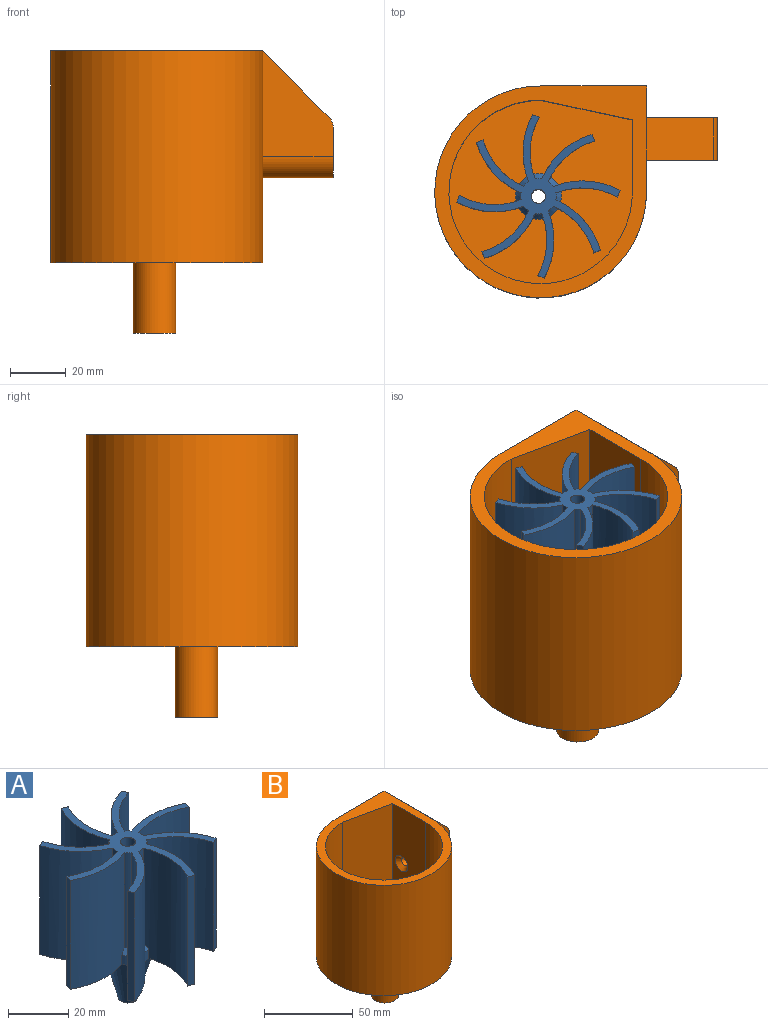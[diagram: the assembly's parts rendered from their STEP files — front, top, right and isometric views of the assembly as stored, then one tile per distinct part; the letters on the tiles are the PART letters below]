
ASSEMBLY  parts=2 mates=1
PART A: 60 faces, bbox 58.7x58.7x63.5 mm
  f0: cylinder r=28.57mm len=44.45mm, axis (0,0,-1), area 1098.7mm2, adj f18,f30,f31,f33,f48,f53
  f1: cylinder r=26.04mm len=44.45mm, axis (0,0,-1), area 1014.1mm2, adj f18,f24,f31,f33,f47,f54
  f2: cylinder r=28.57mm len=44.45mm, axis (0,0,-1), area 1098.7mm2, adj f29,f31,f34,f41,f49,f58
  f3: cylinder r=26.04mm len=44.45mm, axis (0,0,-1), area 1014.1mm2, adj f23,f31,f34,f41,f45,f57
  f4: cylinder r=28.57mm len=44.45mm, axis (0,0,-1), area 1098.7mm2, adj f20,f28,f31,f35,f46,f55
  f5: cylinder r=26.04mm len=44.45mm, axis (0,0,-1), area 1014.1mm2, adj f20,f27,f31,f35,f51,f56
  f6: cylinder r=28.57mm len=44.45mm, axis (0,0,-1), area 1098.7mm2, adj f21,f27,f31,f36,f51,f56
  f7: cylinder r=26.04mm len=44.45mm, axis (0,0,-1), area 1014.1mm2, adj f21,f26,f31,f36,f50,f59
  f8: cylinder r=28.57mm len=44.45mm, axis (0,0,-1), area 1098.7mm2, adj f22,f26,f31,f37,f50,f59
  f9: cylinder r=26.04mm len=44.45mm, axis (0,0,-1), area 1014.1mm2, adj f22,f29,f31,f37,f49,f58
  f10: cylinder r=28.57mm len=44.45mm, axis (0,0,-1), area 1098.7mm2, adj f17,f25,f31,f38,f44,f52
  f11: cylinder r=26.04mm len=44.45mm, axis (0,0,-1), area 1014.1mm2, adj f17,f30,f31,f38,f48,f53
  f12: cylinder r=28.57mm len=44.45mm, axis (0,0,-1), area 1098.7mm2, adj f19,f24,f31,f39,f47,f54
  f13: cylinder r=26.04mm len=44.45mm, axis (0,0,-1), area 1014.1mm2, adj f19,f28,f31,f39,f46,f55
  f14: cylinder r=28.57mm len=44.45mm, axis (0,0,-1), area 1098.7mm2, adj f16,f23,f31,f40,f45,f57
  f15: cylinder r=26.04mm len=44.45mm, axis (0,0,-1), area 1014.1mm2, adj f16,f25,f31,f40,f44,f52
  f16: plane 18.28x15.27mm, normal (0,0,-1), area 55.8mm2, adj f14,f15,f40,f43
  f17: plane 22.26x5.84mm, normal (0,0,-1), area 55.8mm2, adj f10,f11,f38,f43
  f18: plane 18.28x15.27mm, normal (0,0,-1), area 55.8mm2, adj f0,f1,f33,f43
  f19: plane 22.26x5.84mm, normal (0,0,-1), area 55.8mm2, adj f12,f13,f39,f43
  f20: plane 18.28x15.27mm, normal (0,0,-1), area 55.8mm2, adj f4,f5,f35,f43
  f21: plane 22.26x5.84mm, normal (0,0,-1), area 55.8mm2, adj f6,f7,f36,f43
  f22: plane 18.28x15.27mm, normal (0,0,-1), area 55.8mm2, adj f8,f9,f37,f43
  f23: cylinder r=6.35mm len=38.74mm, axis (0,0,-1), area 94.1mm2, adj f3,f14,f31,f57
  f24: cylinder r=6.35mm len=38.74mm, axis (0,0,-1), area 94.1mm2, adj f1,f12,f31,f54
  f25: cylinder r=6.35mm len=38.74mm, axis (0,0,-1), area 94.1mm2, adj f10,f15,f31,f52
  f26: cylinder r=6.35mm len=38.74mm, axis (0,0,-1), area 94.1mm2, adj f7,f8,f31,f59
  f27: cylinder r=6.35mm len=38.74mm, axis (0,0,-1), area 94.1mm2, adj f5,f6,f31,f56
  f28: cylinder r=6.35mm len=38.74mm, axis (0,0,-1), area 94.1mm2, adj f4,f13,f31,f55
  f29: cylinder r=6.35mm len=38.74mm, axis (0,0,-1), area 94.1mm2, adj f2,f9,f31,f58
  f30: cylinder r=6.35mm len=38.74mm, axis (0,0,-1), area 94.1mm2, adj f0,f11,f31,f53
  f31: plane 58.74x58.74mm, normal (0,0,1), area 591.8mm2, adj f0,f1,f2,f3,f4,f5,f6,f7
  f32: cylinder r=2.54mm len=63.5mm, axis (0,0,1), area 1013.4mm2, adj f31,f42
  f33: plane 44.45x2.34mm, normal (0.91,0.41,0), area 114mm2, adj f0,f1,f18,f31
  f34: plane 44.45x2.4mm, normal (-0.94,0.35,0), area 114mm2, adj f2,f3,f31,f41
  f35: plane 44.45x2.34mm, normal (0.41,-0.91,0), area 114mm2, adj f4,f5,f20,f31
  f36: plane 44.45x2.4mm, normal (-0.35,-0.94,0), area 114mm2, adj f6,f7,f21,f31
  f37: plane 44.45x2.34mm, normal (-0.91,-0.41,0), area 114mm2, adj f8,f9,f22,f31
  f38: plane 44.45x2.4mm, normal (0.35,0.94,0), area 114mm2, adj f10,f11,f17,f31
  f39: plane 44.45x2.4mm, normal (0.94,-0.35,0), area 114mm2, adj f12,f13,f19,f31
  f40: plane 44.45x2.34mm, normal (-0.41,0.91,0), area 114mm2, adj f14,f15,f16,f31
  f41: plane 22.26x5.84mm, normal (0,0,-1), area 55.8mm2, adj f2,f3,f34,f43
  f42: plane 6.35x6.35mm, normal (0,0,-1), area 11.4mm2, adj f32,f43
  f43: cone r=3.17mm half-angle=14.9deg, axis (0,0,1), area 708mm2, adj f16,f17,f18,f19,f20,f21,f22,f41
  f44: cylinder r=8.26mm len=3.81mm, axis (0,0,-1), area 15mm2, adj f10,f15,f43,f52
  f45: cylinder r=8.26mm len=3.89mm, axis (0,0,-1), area 15mm2, adj f3,f14,f43,f57
  f46: cylinder r=8.26mm len=3.89mm, axis (0,0,-1), area 15mm2, adj f4,f13,f43,f55
  f47: cylinder r=8.26mm len=3.81mm, axis (0,0,-1), area 15mm2, adj f1,f12,f43,f54
  f48: cylinder r=8.26mm len=3.89mm, axis (0,0,-1), area 15mm2, adj f0,f11,f43,f53
  f49: cylinder r=8.26mm len=3.81mm, axis (0,0,-1), area 15mm2, adj f2,f9,f43,f58
  f50: cylinder r=8.26mm len=3.89mm, axis (0,0,-1), area 15mm2, adj f7,f8,f43,f59
  f51: cylinder r=8.26mm len=3.81mm, axis (0,0,-1), area 15mm2, adj f5,f6,f43,f56
  f52: cone r=5.71mm half-angle=45deg, axis (0,0,-1), area 8.5mm2, adj f10,f15,f25,f44
  f53: cone r=5.71mm half-angle=45deg, axis (0,0,-1), area 8.5mm2, adj f0,f11,f30,f48
  f54: cone r=5.71mm half-angle=45deg, axis (0,0,-1), area 8.5mm2, adj f1,f12,f24,f47
  f55: cone r=5.71mm half-angle=45deg, axis (0,0,-1), area 8.5mm2, adj f4,f13,f28,f46
  f56: cone r=5.71mm half-angle=45deg, axis (0,0,-1), area 8.5mm2, adj f5,f6,f27,f51
  f57: cone r=5.71mm half-angle=45deg, axis (0,0,-1), area 8.5mm2, adj f3,f14,f23,f45
  f58: cone r=5.71mm half-angle=45deg, axis (0,0,-1), area 8.5mm2, adj f2,f9,f29,f49
  f59: cone r=5.71mm half-angle=45deg, axis (0,0,-1), area 8.5mm2, adj f7,f8,f26,f50
PART B: 22 faces, bbox 101.6x76.2x101.7 mm
  f0: plane 76.2x38.1mm, normal (1,0,0), area 2231.4mm2, adj f1,f3,f4,f5,f6,f17,f18
  f1: cylinder r=7.62mm len=25.4mm, axis (-1,0,0), area 608mm2, adj f0,f7,f17,f18
  f2: plane 71.12x25.91mm, normal (-1,0,0), area 1761.5mm2, adj f4,f9,f10,f14,f16
  f3: plane 76.2x38.1mm, normal (0,1,0), area 2903.2mm2, adj f0,f4,f5,f6
  f4: plane 76.2x76.2mm, normal (0,0,1), area 1330mm2, adj f0,f2,f3,f6,f9,f16,f19
  f5: plane 76.2x76.2mm, normal (0,0,-1), area 4689.5mm2, adj f0,f3,f6,f11
  f6: cylinder r=38.1mm len=76.2mm, axis (0,0,1), area 13681.1mm2, adj f0,f3,f4,f5
  f7: plane 18.27x15.24mm, normal (1,0,0), area 233.3mm2, adj f1,f8,f17,f18,f21
  f8: cylinder r=2.54mm len=27.94mm, axis (1,0,0), area 445.9mm2, adj f7,f14
  f9: cylinder r=33.02mm len=71.12mm, axis (0,0,1), area 11066.5mm2, adj f2,f4,f10,f16
  f10: plane 66.04x66.04mm, normal (0,0,1), area 3460.8mm2, adj f2,f9,f15,f16
  f11: cylinder r=7.62mm len=25.4mm, axis (0,0,1), area 1216.1mm2, adj f5,f12
  f12: plane 15.24x15.24mm, normal (0,0,-1), area 162.1mm2, adj f11,f13
  f13: cylinder r=2.54mm len=27.94mm, axis (0,0,-1), area 445.9mm2, adj f12,f15
  f14: cone r=2.54mm half-angle=45deg, axis (-1,0,0), area 86mm2, adj f2,f8
  f15: cone r=5.08mm half-angle=45deg, axis (0,0,1), area 86mm2, adj f10,f13
  f16: plane 71.12x33.02mm, normal (-0.21,-0.98,0), area 2402.2mm2, adj f2,f4,f9,f10
  f17: plane 38.16x25.4mm, normal (0,-1,0), area 646mm2, adj f0,f1,f7,f19,f20,f21
  f18: plane 38.16x25.4mm, normal (0,1,0), area 646mm2, adj f0,f1,f7,f19,f20,f21
  f19: plane 15.24x0.06mm, normal (-1,0,0), area 0.9mm2, adj f4,f17,f18,f20
  f20: plane 23.91x23.91mm, normal (0.71,0,0.71), area 515.4mm2, adj f17,f18,f19,f21
  f21: cylinder r=5.08mm len=15.24mm, axis (0,-1,0), area 60.8mm2, adj f7,f17,f18,f20
PLACE A rot(axis=(0,0,1),180deg) t=(-72.23,72.65,27.01)mm
PLACE B t=(-9.45,31.45,20.66)mm
MATE revolute A.f23 <-> B.f13  axis (0,0,1) through (-9.45,31.45,96.86)mm
